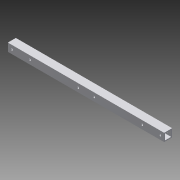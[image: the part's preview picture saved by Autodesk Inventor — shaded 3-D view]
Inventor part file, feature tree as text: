
AUTODESK INVENTOR PART (.ipt)
format: ipt  version: 2015 SP1 (Build 190203100, 203)  size: 169,472 bytes
history: native  units: in
note: dims shown in document units (in); Inventor stores cm internally (conversion verified against a paired STEP export)
features: sketch x7, extrude x4, hole x3, projected_geometry x3
ambient origin geometry x8: Origin, YZ Plane, XZ Plane, XY Plane, X Axis, Y Axis, Z Axis, Center Point
bodies: Solid1 (feature_tree)
feature tree (17):
  extrude  "Extrusion1"  Depth=1.0in
  hole  "Hole1"  [1 undecoded]
  hole  "Hole2"  [1 undecoded]
  hole  "Hole3"  [1 undecoded]
  extrude  "Extrusion2"  Depth=0.5in
  extrude  "Extrusion3"  Depth=1.0in
  extrude  "Extrusion4"  Depth=1.0in
  sketch  "Sketch1"  dims[d0=1.0in d1=1.0in]
  sketch  "Sketch2"  dims[d2=0.75in d3=0.75in]
  projected_geometry  "Projected Loop1"
  sketch  "Sketch3"  dims[d4=0.125in d5=0.125in]
  projected_geometry  "Projected Loop2"
  sketch  "Sketch4"  dims[d6=21.5in d7=0.0in d8=0.5in]
  projected_geometry  "Projected Loop3"
  sketch  "Sketch7"  dims[d9=0.5in d10=0.5in]
  sketch  "Sketch8"  dims[d11=0.5in]
  sketch  "Sketch9"  dims[d12=0.25in d13=0.75in d14=0.375in d15=0.25in d16=0.5635in d17=1.0in d18=0.8108in d19=9.75in d20=9.75in d21=0.5in d22=0.5in d23=0.25in d24=0.75in d25=0.375in d26=0.25in d27=0.5635in d28=1.0in d29=0.8108in d30=1.5in d31=0.5in d32=0.5in d33=1.5in d34=0.1875in d35=0.75in d36=0.375in d37=0.25in d38=0.5635in d39=1.0in d40=0.8108in d65=0.25in d66=0.25in d67=0.5in d68=2.25in d69=0.25in d70=0.25in d71=0.5in d72=2.25in d73=1.0in d74=0.0in d75=1.0in d76=0.0in d77=1.0in d78=0.0in]
note: 3 required parameter values undecoded (feature->parameter linkage not recoverable at this tier; creation-order binding heuristic only, values carry confidence <= 0.55)
